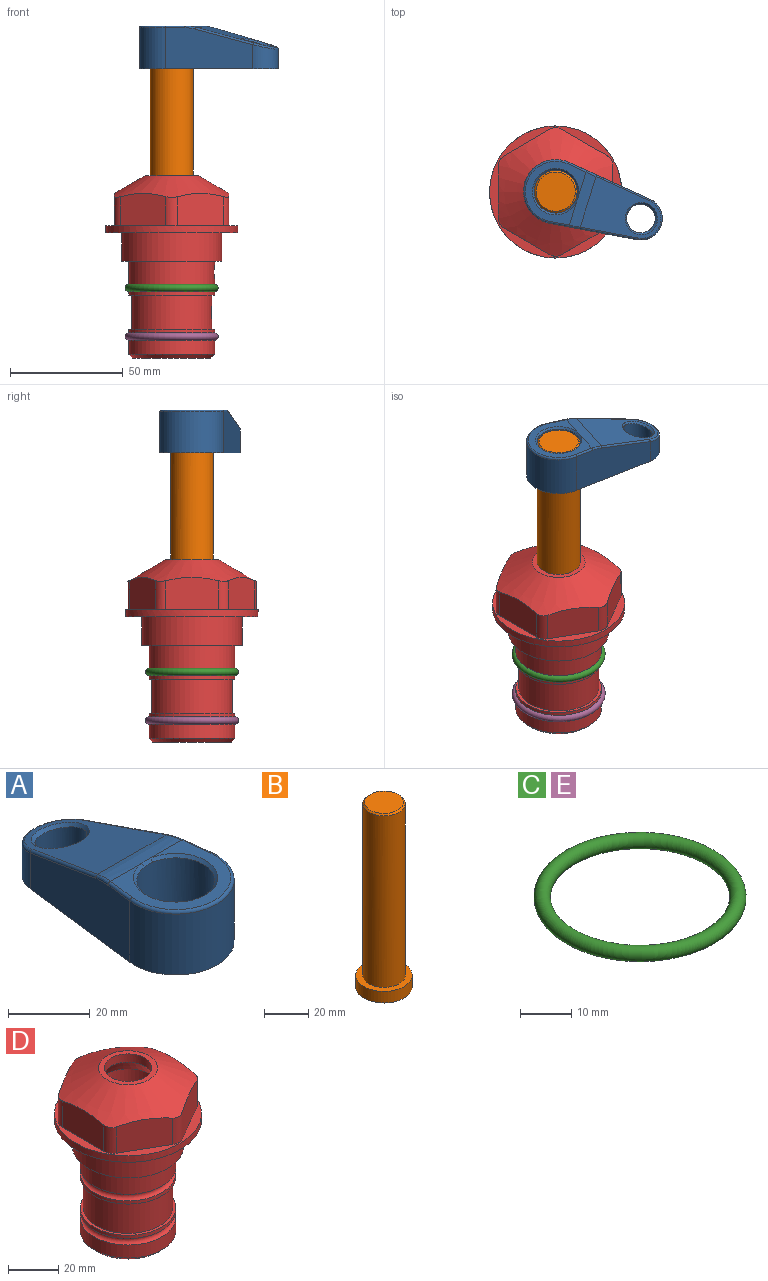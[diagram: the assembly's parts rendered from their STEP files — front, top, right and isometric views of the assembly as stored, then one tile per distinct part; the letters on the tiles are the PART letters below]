
ASSEMBLY  parts=5 mates=4
PART A: 31 faces, bbox 31.7x65.5x19.8 mm
  f0: plane 39.12x18.26mm, normal (0.99,0.12,0), area 612.2mm2, adj f1,f4,f7,f11,f13,f15
  f1: cylinder r=9.53mm len=18.91mm, axis (0,0,-1), area 296.1mm2, adj f0,f2,f7,f17
  f2: plane 39.12x18.26mm, normal (-0.99,0.12,0), area 612.2mm2, adj f1,f4,f7,f12,f14,f16
  f3: cylinder r=6.35mm len=12.7mm, axis (0,0,-1), area 362.4mm2, adj f7,f18
  f4: cylinder r=14.29mm len=28.58mm, axis (0,0,-1), area 882.2mm2, adj f0,f2,f7,f10
  f5: cylinder r=9.53mm len=19.05mm, axis (0,0,-1), area 1092.6mm2, adj f7,f19,f20
  f6: plane 26.99x23.69mm, normal (0,0,1), area 216.2mm2, adj f9,f10,f11,f12,f19
  f7: plane 63.5x28.58mm, normal (0,0,-1), area 661.8mm2, adj f0,f1,f2,f3,f4,f5,f22,f23
  f8: plane 33.52x23.6mm, normal (0,0.26,0.97), area 486mm2, adj f9,f15,f16,f17,f18
  f9: cylinder r=19.05mm len=24.72mm, axis (1,0,0), area 120.4mm2, adj f6,f8,f13,f14,f20
  f10: torus R=13.49mm, axis (0,0,1), area 59mm2, adj f4,f6,f11,f12
  f11: cylinder r=0.79mm len=8.67mm, axis (0.12,-0.99,0), area 10.8mm2, adj f0,f6,f10,f13
  f12: cylinder r=0.79mm len=8.67mm, axis (0.12,0.99,0), area 10.8mm2, adj f2,f6,f10,f14
  f13: bspline ~4.95x1.42mm, area 6.1mm2, adj f0,f9,f11,f15
  f14: bspline ~4.95x1.42mm, area 6.1mm2, adj f2,f9,f12,f16
  f15: cylinder r=0.79mm len=25.95mm, axis (0.12,-0.96,0.26), area 32.9mm2, adj f0,f8,f13,f17
  f16: cylinder r=0.79mm len=25.95mm, axis (0.12,0.96,-0.26), area 32.9mm2, adj f2,f8,f14,f17
  f17: bspline ~18.91x8.38mm, area 30mm2, adj f1,f8,f15,f16
  f18: bspline ~14.29x14.29mm, area 48.3mm2, adj f3,f8
  f19: cone r=9.53mm half-angle=45deg, axis (0,0,1), area 66.5mm2, adj f5,f6,f20
  f20: bspline ~3.22x0.96mm, area 3.5mm2, adj f5,f9,f19
  f21: plane 2.75x2.72mm, normal (0,0,-1), area 2.9mm2, adj f23,f25,f28
  f22: plane 23.05x15.88mm, normal (-0.99,-0.12,0), area 323.6mm2, adj f7,f25,f26,f27,f28,f29
  f23: plane 23.05x15.88mm, normal (0.99,-0.12,0), area 323.6mm2, adj f7,f21,f25,f27,f28,f30
  f24: cylinder r=9.53mm len=10.69mm, axis (0,0,-1), area 114.7mm2, adj f7,f27,f29,f30
  f25: cylinder r=12.7mm len=20.59mm, axis (0,0,-1), area 381.1mm2, adj f7,f21,f22,f23,f26,f28
  f26: plane 2.75x2.72mm, normal (0,0,-1), area 2.9mm2, adj f22,f25,f28
  f27: plane 19.72x18.37mm, normal (0,-0.26,-0.97), area 291.8mm2, adj f22,f23,f24,f28,f29,f30
  f28: cylinder r=15.88mm len=19.92mm, axis (1,0,0), area 54.8mm2, adj f21,f22,f23,f25,f26,f27
  f29: cylinder r=1.59mm len=11mm, axis (0,0,-1), area 34.7mm2, adj f7,f22,f24,f27
  f30: cylinder r=1.59mm len=11mm, axis (0,0,-1), area 34.7mm2, adj f7,f23,f24,f27
PART B: 6 faces, bbox 25.4x25.4x101.6 mm
  f0: plane 17.46x17.46mm, normal (0,0,1), area 239.5mm2, adj f5
  f1: plane 25.4x25.4mm, normal (0,0,-1), area 506.7mm2, adj f2
  f2: cylinder r=12.7mm len=25.4mm, axis (0,0,1), area 506.7mm2, adj f1,f3
  f3: plane 25.4x25.4mm, normal (0,0,1), area 221.7mm2, adj f2,f4
  f4: cylinder r=9.53mm len=94.46mm, axis (0,0,1), area 5653mm2, adj f3,f5
  f5: cone r=8.73mm half-angle=45deg, axis (0,0,-1), area 64.4mm2, adj f0,f4
PART C: 1 faces, bbox 44.7x44.7x3.2 mm
  f0: torus R=19.05mm, axis (0,0,1), area 1193.9mm2
PART D: 36 faces, bbox 58.7x58.7x81 mm
  f0: cylinder r=17.78mm len=35.56mm, axis (0,0,1), area 1670.8mm2, adj f23,f24,f31
  f1: cylinder r=19.05mm len=38.1mm, axis (0,0,1), area 1191.9mm2, adj f26,f27,f30
  f2: plane 58.66x58.66mm, normal (0,0,-1), area 1150.6mm2, adj f3,f28
  f3: cylinder r=29.33mm len=58.66mm, axis (0,0,-1), area 585.1mm2, adj f2,f4
  f4: plane 58.66x58.66mm, normal (0,0,1), area 475.9mm2, adj f3,f5,f6,f7,f8,f9,f10,f11
  f5: plane 20.32x14.34mm, normal (-0.5,0.87,0), area 324.4mm2, adj f4,f15,f16,f17
  f6: plane 20.32x14.34mm, normal (0.5,0.87,0), area 324.4mm2, adj f4,f14,f15,f17
  f7: plane 23.48x14.34mm, normal (1,0,0), area 324.4mm2, adj f4,f13,f14,f17
  f8: plane 20.32x14.34mm, normal (0.5,-0.87,0), area 324.4mm2, adj f4,f12,f13,f17
  f9: plane 20.32x14.34mm, normal (-0.5,-0.87,0), area 324.4mm2, adj f4,f11,f12,f17
  f10: plane 23.48x14.34mm, normal (-1,0,0), area 324.4mm2, adj f4,f11,f16,f17
  f11: cylinder r=5.08mm len=12.85mm, axis (0,0,-1), area 67.2mm2, adj f4,f9,f10,f17
  f12: cylinder r=5.08mm len=12.85mm, axis (0,0,-1), area 67.2mm2, adj f4,f8,f9,f17
  f13: cylinder r=5.08mm len=12.85mm, axis (0,0,-1), area 67.2mm2, adj f4,f7,f8,f17
  f14: cylinder r=5.08mm len=12.85mm, axis (0,0,-1), area 67.2mm2, adj f4,f6,f7,f17
  f15: cylinder r=5.08mm len=12.85mm, axis (0,0,-1), area 67.2mm2, adj f4,f5,f6,f17
  f16: cylinder r=5.08mm len=12.85mm, axis (0,0,-1), area 67.2mm2, adj f4,f5,f10,f17
  f17: cone r=11.73mm half-angle=60deg, axis (0,0,-1), area 2071.8mm2, adj f5,f6,f7,f8,f9,f10,f11,f12
  f18: plane 23.46x23.46mm, normal (0,0,1), area 147.4mm2, adj f17,f35
  f19: plane 34.93x34.93mm, normal (0,0,-1), area 958mm2, adj f29
  f20: cylinder r=19.05mm len=38.1mm, axis (0,0,1), area 760.1mm2, adj f21,f29
  f21: torus R=19.05mm, axis (0,0,1), area 565.3mm2, adj f20,f22
  f22: cylinder r=19.05mm len=38.1mm, axis (0,0,1), area 190mm2, adj f21,f23
  f23: plane 38.1x38.1mm, normal (0,0,1), area 146.9mm2, adj f0,f22
  f24: plane 38.1x38.1mm, normal (0,0,-1), area 146.9mm2, adj f0,f25
  f25: cylinder r=19.05mm len=38.1mm, axis (0,0,1), area 190mm2, adj f24,f26
  f26: torus R=19.05mm, axis (0,0,1), area 565.3mm2, adj f1,f25
  f27: plane 44.45x44.45mm, normal (0,0,-1), area 411.7mm2, adj f1,f28
  f28: cylinder r=22.23mm len=44.45mm, axis (0,0,1), area 1773.5mm2, adj f2,f27
  f29: cone r=19.05mm half-angle=45deg, axis (0,0,1), area 257.5mm2, adj f19,f20
  f30: cylinder r=3.17mm len=6.75mm, axis (-1,0,0), area 128mm2, adj f1,f33
  f31: cylinder r=3.17mm len=6.35mm, axis (-1,0,0), area 102.5mm2, adj f0,f33
  f32: plane 25.4x25.4mm, normal (0,0,1), area 506.7mm2, adj f33
  f33: cylinder r=12.7mm len=66.42mm, axis (0,0,-1), area 5236.2mm2, adj f30,f31,f32,f34
  f34: cone r=9.53mm half-angle=30deg, axis (0,0,-1), area 443.4mm2, adj f33,f35
  f35: cylinder r=9.53mm len=19.05mm, axis (0,0,-1), area 240.9mm2, adj f18,f34
PART E: same geometry as C
PLACE A rot(axis=(0,0,-1),107.5deg) t=(0,0,28.35)mm
PLACE B rot(axis=(0,0,-1),107.5deg) t=(0,0,27.55)mm
PLACE C at identity
PLACE D at identity fixed
PLACE E t=(0,0,-21.59)mm
MATE fastened C.f0 <-> D.f0  axis (0,0,1) through (0,0,-24.51)mm
MATE fastened E.f0 <-> D.f0  axis (0,0,1) through (0,0,-46.1)mm
MATE fastened B.f2 <-> A.f4  axis (0,0,1) through (0,0,91.05)mm
MATE cylindrical D.f0 <-> B.f2  axis (0,0,1) through (0,0,-50.55)mm
